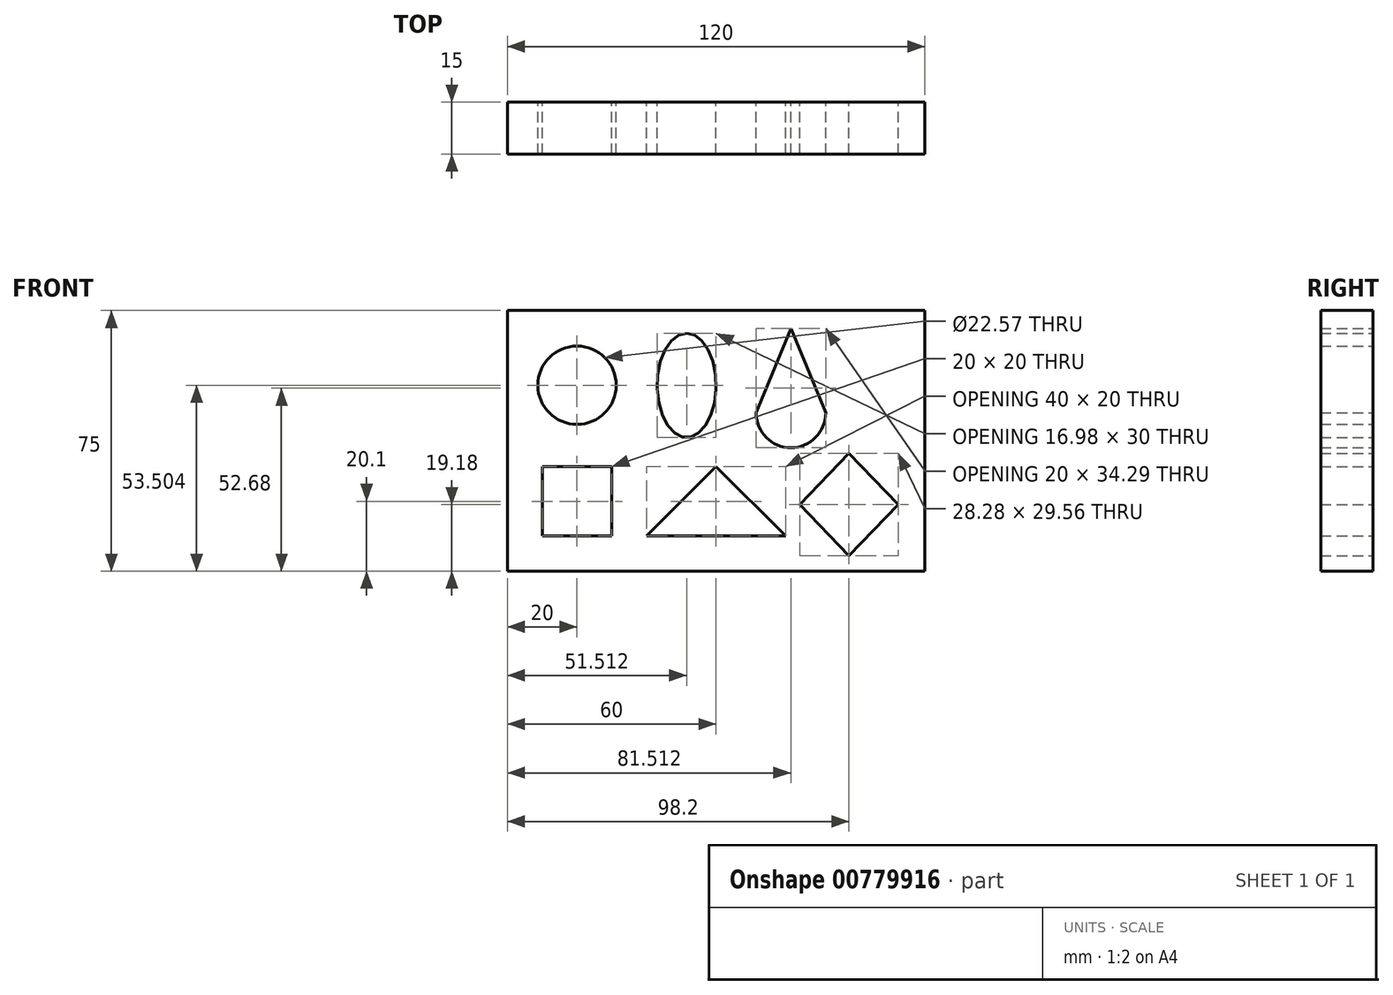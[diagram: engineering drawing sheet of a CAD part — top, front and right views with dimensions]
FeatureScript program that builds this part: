
annotation { "Feature Type Name" : "Feature", "Feature Type Description" : "" }
export const myFeature = defineFeature(function(context is Context, id is Id, definition is map)
    precondition{}
    {
        {
            var Q0;
            Q0=qCreatedBy(makeId("Front.planeOp"),FACE);
            var sketch = newSketch(context, id + "F0", { "sketchPlane" : qUnion([Q0])});
            skLineSegment(sketch, "E0.bottom", {"start": v(-60, 25) * mm, "end": v(60, 25) * mm});
            skLineSegment(sketch, "E0.top", {"start": v(-60, -50) * mm, "end": v(60, -50) * mm});
            skLineSegment(sketch, "E0.left", {"start": v(-60, 25) * mm, "end": v(-60, -50) * mm});
            skLineSegment(sketch, "E0.right", {"start": v(60, 25) * mm, "end": v(60, -50) * mm});
            skLineSegment(sketch, "E1.bottom", {"start": v(-30, -19.9) * mm, "end": v(-50, -19.9) * mm});
            skLineSegment(sketch, "E1.top", {"start": v(-30, -39.9) * mm, "end": v(-50, -39.9) * mm});
            skLineSegment(sketch, "E1.left", {"start": v(-30, -19.9) * mm, "end": v(-30, -39.9) * mm});
            skLineSegment(sketch, "E1.right", {"start": v(-50, -19.9) * mm, "end": v(-50, -39.9) * mm});
            skPoint(sketch, "E1.middle", {"position": v(-40, -29.9) * mm});
            skLineSegment(sketch, "E2", {"start": v(0, -39.9) * mm, "end": v(-20, -39.9) * mm});
            skCircle(sketch, "E3", {"center": v(-40, 3.5) * mm, "radius": 11.28 * mm});
            skEllipse(sketch, "E4", {"center": v(-8.49, 3.5) * mm, "majorRadius": 15 * mm, "minorRadius": 8.49 * mm, "majorAxis": v(0, 1)});
            skPoint(sketch, "E5.endSnap0", {"position": v(-8.49, 18.5) * mm});
            skArc(sketch, "E6", {"start": v(11.51, -4.47) * mm, "mid": v(21.51, -14.47) * mm, "end": v(31.51, -4.47) * mm});
            skLineSegment(sketch, "E7", {"start": v(0, -19.9) * mm, "end": v(-20, -39.9) * mm});
            skLineSegment(sketch, "E8.MirrorCS", {"start": v(0, -39.9) * mm, "end": v(20, -39.9) * mm});
            skLineSegment(sketch, "E9.MirrorCS", {"start": v(0, -19.9) * mm, "end": v(20, -39.9) * mm});
            skLineSegment(sketch, "E10", {"start": v(38.2, -16.04) * mm, "end": v(24.06, -30.82) * mm});
            skLineSegment(sketch, "E11", {"start": v(52.34, -30.82) * mm, "end": v(38.2, -16.04) * mm});
            skLineSegment(sketch, "E12.MirrorCS", {"start": v(38.2, -45.6) * mm, "end": v(24.06, -30.82) * mm});
            skLineSegment(sketch, "E13.MirrorCS", {"start": v(52.34, -30.82) * mm, "end": v(38.2, -45.6) * mm});
            skLineSegment(sketch, "E14", {"start": v(11.51, -4.47) * mm, "end": v(21.51, 19.83) * mm});
            skLineSegment(sketch, "E15", {"start": v(21.51, 19.83) * mm, "end": v(31.51, -4.47) * mm});
            skSolve(sketch);
        }
        {
            var Q0;
            Q0=makeQuery(id+"F0.imprint","IMPRINT",FACE,{"disambiguationData":[TD([[makeQuery(id+"F0.imprint","IMPRINT",EDGE,{"derivedFrom":sQuery(id+"F0.wireOp",EDGE,"E0.bottom")}),-1.0]])]});
            extrude(context, id + "F1", {"entities" : qUnion([Q0]), "endBound" : BoundingType.SYMMETRIC, "depth" : 15 * mm, "offsetDistance" : 25 * mm});
        }
    });
